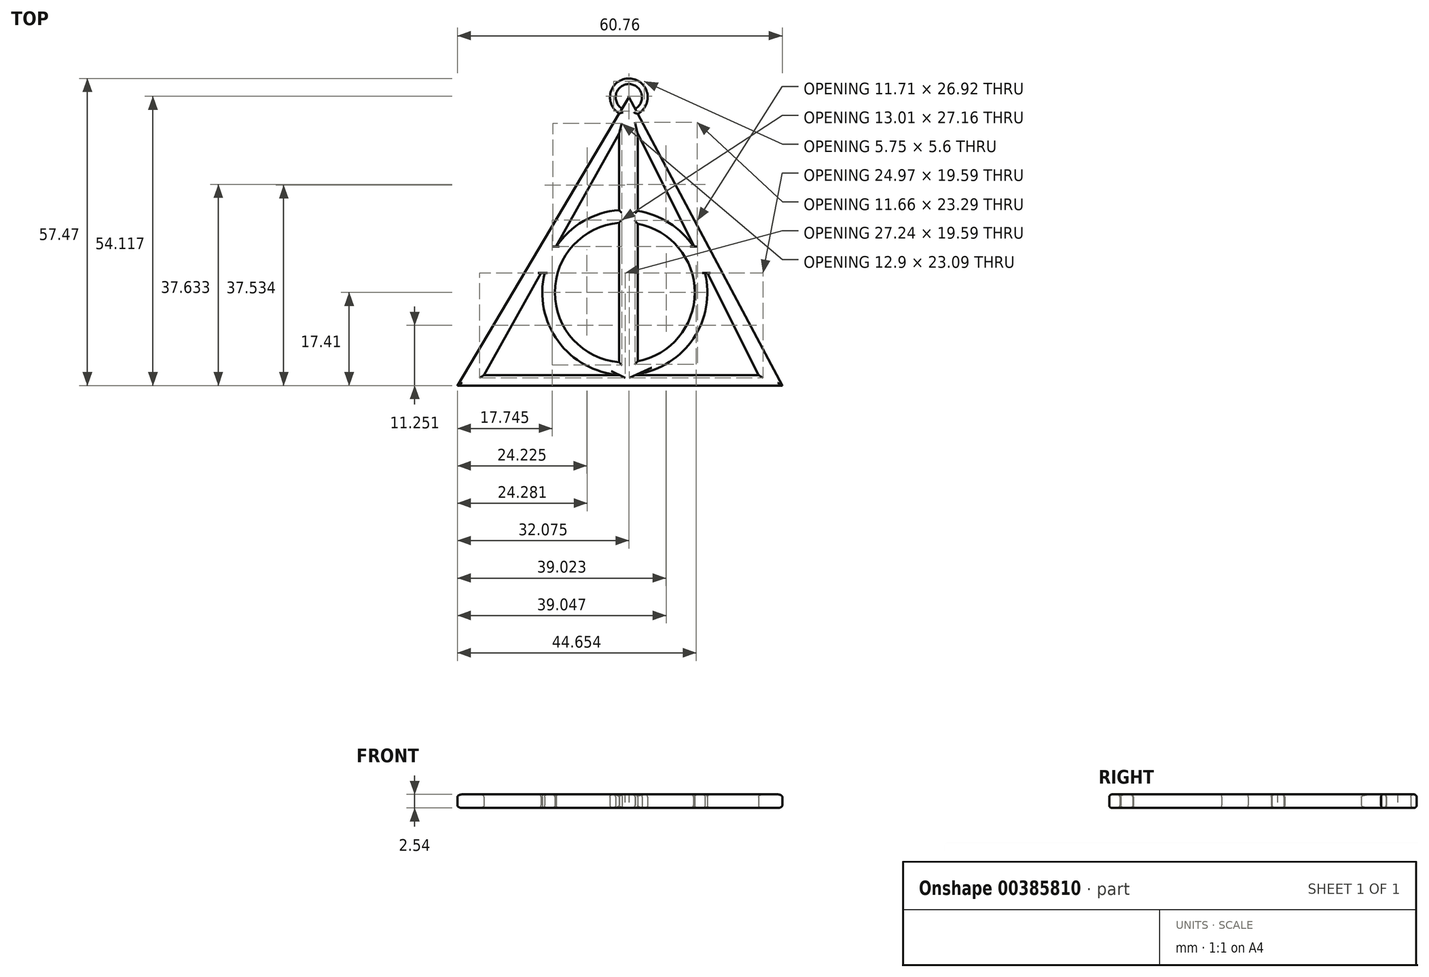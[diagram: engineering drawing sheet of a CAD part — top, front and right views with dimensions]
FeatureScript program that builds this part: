
annotation { "Feature Type Name" : "Feature", "Feature Type Description" : "" }
export const myFeature = defineFeature(function(context is Context, id is Id, definition is map)
    precondition{}
    {
        {
            var Q0;
            Q0=qCreatedBy(makeId("Top.planeOp"),FACE);
            var sketch = newSketch(context, id + "F0", { "sketchPlane" : qUnion([Q0])});
            skArc(sketch, "E0", {"start": v(0.01, 14.02) * mm, "mid": v(0, 14.02) * mm, "end": v(-0.02, 14.02) * mm});
            skLineSegment(sketch, "E1", {"start": v(0, 14.05) * mm, "end": v(-0.02, 14.02) * mm});
            skLineSegment(sketch, "E2", {"start": v(0.01, 14.02) * mm, "end": v(0, 14.05) * mm});
            skPoint(sketch, "E3.orphan", {"position": v(0, 12.28) * mm});
            skPoint(sketch, "E4.start.orphan", {"position": v(0.45, 11.3) * mm});
            skPoint(sketch, "E5.start.orphan", {"position": v(-0.48, 11.3) * mm});
            skArc(sketch, "E6", {"start": v(-1.09, 13.04) * mm, "mid": v(-13.08, 0) * mm, "end": v(-1.09, -13.04) * mm});
            skArc(sketch, "E7", {"start": v(-1.09, 15.4) * mm, "mid": v(-7.76, 13.36) * mm, "end": v(-12.84, 8.58) * mm});
            skLineSegment(sketch, "E8", {"start": v(1.98, -15.44) * mm, "end": v(25, -15.44) * mm});
            skLineSegment(sketch, "E9", {"start": v(25, -15.44) * mm, "end": v(15.45, 3.63) * mm});
            skLineSegment(sketch, "E10", {"start": v(-1.09, 29.72) * mm, "end": v(-12.9, 8.58) * mm});
            skLineSegment(sketch, "E11", {"start": v(-26.32, -15.44) * mm, "end": v(-1, -15.44) * mm});
            skLineSegment(sketch, "E12", {"start": v(0.75, 36.53) * mm, "end": v(1.9, 34.36) * mm});
            skLineSegment(sketch, "E13", {"start": v(29.45, -17.41) * mm, "end": v(-31.31, -17.41) * mm});
            skLineSegment(sketch, "E14", {"start": v(-31.31, -17.41) * mm, "end": v(-1.05, 33.5) * mm});
            skLineSegment(sketch, "E15", {"start": v(-1.09, 29.72) * mm, "end": v(-1.09, 15.4) * mm});
            skLineSegment(sketch, "E16", {"start": v(2.39, 29.72) * mm, "end": v(2.39, 15.26) * mm});
            skPoint(sketch, "E17.orphan", {"position": v(0.75, 33) * mm});
            skArc(sketch, "E18.trimOffspring", {"start": v(2.39, -12.86) * mm, "mid": v(13.08, 0) * mm, "end": v(2.39, 12.86) * mm});
            skArc(sketch, "E19.trimOffspring", {"start": v(2.39, -15.26) * mm, "mid": v(12.84, -8.58) * mm, "end": v(15.01, 3.63) * mm});
            skLineSegment(sketch, "E20", {"start": v(2.39, -15.26) * mm, "end": v(1.98, -15.44) * mm});
            skLineSegment(sketch, "E21.trimOffspring", {"start": v(-1.09, 13.04) * mm, "end": v(-1.09, -13.04) * mm});
            skLineSegment(sketch, "E22.trimOffspring", {"start": v(2.39, 12.86) * mm, "end": v(2.39, -12.86) * mm});
            skLineSegment(sketch, "E23", {"start": v(-1.09, -15.4) * mm, "end": v(-1, -15.44) * mm});
            skPoint(sketch, "E24.orphan", {"position": v(0, -15.44) * mm});
            skArc(sketch, "E25", {"start": v(1.9, 34.36) * mm, "mid": v(0.8, 39) * mm, "end": v(-0.51, 34.41) * mm});
            skArc(sketch, "E26", {"start": v(2.4, 33.42) * mm, "mid": v(0.83, 40.06) * mm, "end": v(-1.05, 33.5) * mm});
            skLineSegment(sketch, "E27.trimOffspring", {"start": v(-0.51, 34.41) * mm, "end": v(0.75, 36.53) * mm});
            skLineSegment(sketch, "E28.trimOffspring", {"start": v(2.4, 33.42) * mm, "end": v(29.45, -17.41) * mm});
            skLineSegment(sketch, "E29", {"start": v(-12.9, 8.58) * mm, "end": v(-12.84, 8.58) * mm});
            skLineSegment(sketch, "E30", {"start": v(15.45, 3.63) * mm, "end": v(15.01, 3.63) * mm});
            skArc(sketch, "E31.trimOffspring", {"start": v(12.84, 8.58) * mm, "mid": v(8.32, 13.01) * mm, "end": v(2.39, 15.26) * mm});
            skLineSegment(sketch, "E32.trimOffspring", {"start": v(12.98, 8.58) * mm, "end": v(2.39, 29.72) * mm});
            skPoint(sketch, "E33.orphan", {"position": v(22.71, 8.58) * mm});
            skPoint(sketch, "E34.orphan", {"position": v(22.71, 3.63) * mm});
            skLineSegment(sketch, "E35.trimOffspring", {"start": v(12.84, 8.58) * mm, "end": v(12.98, 8.58) * mm});
            skArc(sketch, "E36.trimOffspring", {"start": v(-15.01, 3.63) * mm, "mid": v(-12.47, -9.12) * mm, "end": v(-1.09, -15.4) * mm});
            skLineSegment(sketch, "E37.trimOffspring", {"start": v(-15.01, 3.63) * mm, "end": v(-15.66, 3.63) * mm});
            skLineSegment(sketch, "E38.trimOffspring", {"start": v(-15.66, 3.63) * mm, "end": v(-26.32, -15.44) * mm});
            skSolve(sketch);
        }
        {
            var Q0;
            Q0=makeQuery(id+"F0.imprint","IMPRINT",FACE,{"disambiguationData":[TD([[makeQuery(id+"F0.imprint","IMPRINT",EDGE,{"derivedFrom":sQuery(id+"F0.wireOp",EDGE,"E0")}),1.0]])]});
            extrude(context, id + "F1", {"entities" : qUnion([Q0]), "depth" : 2.54 * mm});
        }
        {
            var Q0;
            Q0=makeQuery(id+"F1.opExtrude","CAP_EDGE",EDGE,{"disambiguationData":[OSD([sQuery(id+"F0.wireOp",EDGE,"E28.trimOffspring")])],"isStart":false});
            var Q1;
            Q1=makeQuery(id+"F1.opExtrude","CAP_EDGE",EDGE,{"disambiguationData":[OSD([sQuery(id+"F0.wireOp",EDGE,"E13")])],"isStart":false});
            var Q2;
            Q2=makeQuery(id+"F1.opExtrude","CAP_EDGE",EDGE,{"disambiguationData":[OSD([sQuery(id+"F0.wireOp",EDGE,"E14")])],"isStart":false});
            var Q3;
            Q3=makeQuery(id+"F1.opExtrude","CAP_EDGE",EDGE,{"disambiguationData":[OSD([sQuery(id+"F0.wireOp",EDGE,"E8")])],"isStart":false});
            var Q4;
            Q4=makeQuery(id+"F1.opExtrude","CAP_EDGE",EDGE,{"disambiguationData":[OSD([sQuery(id+"F0.wireOp",EDGE,"E9")])],"isStart":false});
            var Q5;
            Q5=makeQuery(id+"F1.opExtrude","CAP_EDGE",EDGE,{"disambiguationData":[OSD([sQuery(id+"F0.wireOp",EDGE,"E11")])],"isStart":false});
            var Q6;
            Q6=makeQuery(id+"F1.opExtrude","CAP_EDGE",EDGE,{"disambiguationData":[OSD([sQuery(id+"F0.wireOp",EDGE,"E21.trimOffspring")])],"isStart":false});
            var Q7;
            Q7=makeQuery(id+"F1.opExtrude","CAP_EDGE",EDGE,{"disambiguationData":[OSD([sQuery(id+"F0.wireOp",EDGE,"E6")])],"isStart":false});
            var Q8;
            Q8=makeQuery(id+"F1.opExtrude","CAP_EDGE",EDGE,{"disambiguationData":[OSD([sQuery(id+"F0.wireOp",EDGE,"E18.trimOffspring")])],"isStart":false});
            var Q9;
            Q9=makeQuery(id+"F1.opExtrude","CAP_EDGE",EDGE,{"disambiguationData":[OSD([sQuery(id+"F0.wireOp",EDGE,"E22.trimOffspring")])],"isStart":false});
            var Q10;
            Q10=makeQuery(id+"F1.opExtrude","CAP_EDGE",EDGE,{"disambiguationData":[OSD([sQuery(id+"F0.wireOp",EDGE,"E16")])],"isStart":false});
            var Q11;
            Q11=makeQuery(id+"F1.opExtrude","CAP_EDGE",EDGE,{"disambiguationData":[OSD([sQuery(id+"F0.wireOp",EDGE,"E10")])],"isStart":false});
            var Q12;
            Q12=makeQuery(id+"F1.opExtrude","CAP_EDGE",EDGE,{"disambiguationData":[OSD([sQuery(id+"F0.wireOp",EDGE,"E7")])],"isStart":true});
            var Q13;
            Q13=makeQuery(id+"F1.opExtrude","CAP_EDGE",EDGE,{"disambiguationData":[OSD([sQuery(id+"F0.wireOp",EDGE,"E7")])],"isStart":false});
            var Q14;
            Q14=makeQuery(id+"F1.opExtrude","CAP_EDGE",EDGE,{"disambiguationData":[OSD([sQuery(id+"F0.wireOp",EDGE,"E31.trimOffspring")])],"isStart":false});
            var Q15;
            Q15=makeQuery(id+"F1.opExtrude","CAP_EDGE",EDGE,{"disambiguationData":[OSD([sQuery(id+"F0.wireOp",EDGE,"E38.trimOffspring")])],"isStart":false});
            var Q16;
            Q16=makeQuery(id+"F1.opExtrude","CAP_EDGE",EDGE,{"disambiguationData":[OSD([sQuery(id+"F0.wireOp",EDGE,"E19.trimOffspring")])],"isStart":false});
            var Q17;
            Q17=makeQuery(id+"F1.opExtrude","CAP_EDGE",EDGE,{"disambiguationData":[OSD([sQuery(id+"F0.wireOp",EDGE,"E36.trimOffspring")])],"isStart":false});
            var Q18;
            Q18=makeQuery(id+"F1.opExtrude","CAP_EDGE",EDGE,{"disambiguationData":[OSD([sQuery(id+"F0.wireOp",EDGE,"E32.trimOffspring")])],"isStart":false});
            var Q19;
            Q19=makeQuery(id+"F1.opExtrude","CAP_EDGE",EDGE,{"disambiguationData":[OSD([sQuery(id+"F0.wireOp",EDGE,"E15")])],"isStart":false});
            var Q20;
            Q20=makeQuery(id+"F1.opExtrude","CAP_EDGE",EDGE,{"disambiguationData":[OSD([sQuery(id+"F0.wireOp",EDGE,"E26")])],"isStart":false});
            var Q21;
            Q21=makeQuery(id+"F1.opExtrude","CAP_EDGE",EDGE,{"disambiguationData":[OSD([sQuery(id+"F0.wireOp",EDGE,"E25")])],"isStart":false});
            fillet(context, id + "F2", {"entities" : qUnion([Q0, Q1, Q2, Q3, Q4, Q5, Q6, Q7, Q8, Q9, Q10, Q11, Q12, Q13, Q14, Q15, Q16, Q17, Q18, Q19, Q20, Q21]), "radius" : 0.5 * mm, "tangentPropagation" : true, "allowEdgeOverflow" : false});
        }
        {
            var Q0;
            Q0=makeQuery(id+"F1.opExtrude","CAP_EDGE",EDGE,{"disambiguationData":[OSD([sQuery(id+"F0.wireOp",EDGE,"E31.trimOffspring")])],"isStart":true});
            var Q1;
            Q1=makeQuery(id+"F1.opExtrude","CAP_EDGE",EDGE,{"disambiguationData":[OSD([sQuery(id+"F0.wireOp",EDGE,"E21.trimOffspring")])],"isStart":true});
            var Q2;
            Q2=makeQuery(id+"F1.opExtrude","CAP_EDGE",EDGE,{"disambiguationData":[OSD([sQuery(id+"F0.wireOp",EDGE,"E18.trimOffspring")])],"isStart":true});
            var Q3;
            Q3=makeQuery(id+"F1.opExtrude","CAP_EDGE",EDGE,{"disambiguationData":[OSD([sQuery(id+"F0.wireOp",EDGE,"E6")])],"isStart":true});
            var Q4;
            Q4=makeQuery(id+"F1.opExtrude","CAP_EDGE",EDGE,{"disambiguationData":[OSD([sQuery(id+"F0.wireOp",EDGE,"E22.trimOffspring")])],"isStart":true});
            var Q5;
            Q5=makeQuery(id+"F1.opExtrude","CAP_EDGE",EDGE,{"disambiguationData":[OSD([sQuery(id+"F0.wireOp",EDGE,"E19.trimOffspring")])],"isStart":true});
            var Q6;
            Q6=makeQuery(id+"F1.opExtrude","CAP_EDGE",EDGE,{"disambiguationData":[OSD([sQuery(id+"F0.wireOp",EDGE,"E28.trimOffspring")])],"isStart":true});
            var Q7;
            Q7=makeQuery(id+"F1.opExtrude","CAP_EDGE",EDGE,{"disambiguationData":[OSD([sQuery(id+"F0.wireOp",EDGE,"E16")])],"isStart":true});
            var Q8;
            Q8=makeQuery(id+"F1.opExtrude","CAP_EDGE",EDGE,{"disambiguationData":[OSD([sQuery(id+"F0.wireOp",EDGE,"E8")])],"isStart":true});
            var Q9;
            Q9=makeQuery(id+"F1.opExtrude","CAP_EDGE",EDGE,{"disambiguationData":[OSD([sQuery(id+"F0.wireOp",EDGE,"E9")])],"isStart":true});
            var Q10;
            Q10=makeQuery(id+"F1.opExtrude","CAP_EDGE",EDGE,{"disambiguationData":[OSD([sQuery(id+"F0.wireOp",EDGE,"E13")])],"isStart":true});
            var Q11;
            Q11=makeQuery(id+"F1.opExtrude","CAP_EDGE",EDGE,{"disambiguationData":[OSD([sQuery(id+"F0.wireOp",EDGE,"E36.trimOffspring")])],"isStart":true});
            var Q12;
            Q12=makeQuery(id+"F1.opExtrude","CAP_EDGE",EDGE,{"disambiguationData":[OSD([sQuery(id+"F0.wireOp",EDGE,"E38.trimOffspring")])],"isStart":true});
            var Q13;
            Q13=makeQuery(id+"F1.opExtrude","CAP_EDGE",EDGE,{"disambiguationData":[OSD([sQuery(id+"F0.wireOp",EDGE,"E14")])],"isStart":true});
            var Q14;
            Q14=makeQuery(id+"F1.opExtrude","CAP_EDGE",EDGE,{"disambiguationData":[OSD([sQuery(id+"F0.wireOp",EDGE,"E11")])],"isStart":true});
            var Q15;
            Q15=makeQuery(id+"F1.opExtrude","CAP_EDGE",EDGE,{"disambiguationData":[OSD([sQuery(id+"F0.wireOp",EDGE,"E32.trimOffspring")])],"isStart":true});
            var Q16;
            Q16=makeQuery(id+"F1.opExtrude","CAP_EDGE",EDGE,{"disambiguationData":[OSD([sQuery(id+"F0.wireOp",EDGE,"E26")])],"isStart":true});
            var Q17;
            Q17=makeQuery(id+"F1.opExtrude","CAP_EDGE",EDGE,{"disambiguationData":[OSD([sQuery(id+"F0.wireOp",EDGE,"E25")])],"isStart":true});
            var Q18;
            Q18=makeQuery(id+"F1.opExtrude","CAP_EDGE",EDGE,{"disambiguationData":[OSD([sQuery(id+"F0.wireOp",EDGE,"E10")])],"isStart":true});
            var Q19;
            Q19=makeQuery(id+"F1.opExtrude","CAP_EDGE",EDGE,{"disambiguationData":[OSD([sQuery(id+"F0.wireOp",EDGE,"E15")])],"isStart":true});
            fillet(context, id + "F3", {"entities" : qUnion([Q0, Q1, Q2, Q3, Q4, Q5, Q6, Q7, Q8, Q9, Q10, Q11, Q12, Q13, Q14, Q15, Q16, Q17, Q18, Q19]), "radius" : 0.5 * mm, "tangentPropagation" : true, "allowEdgeOverflow" : false});
        }
    });
